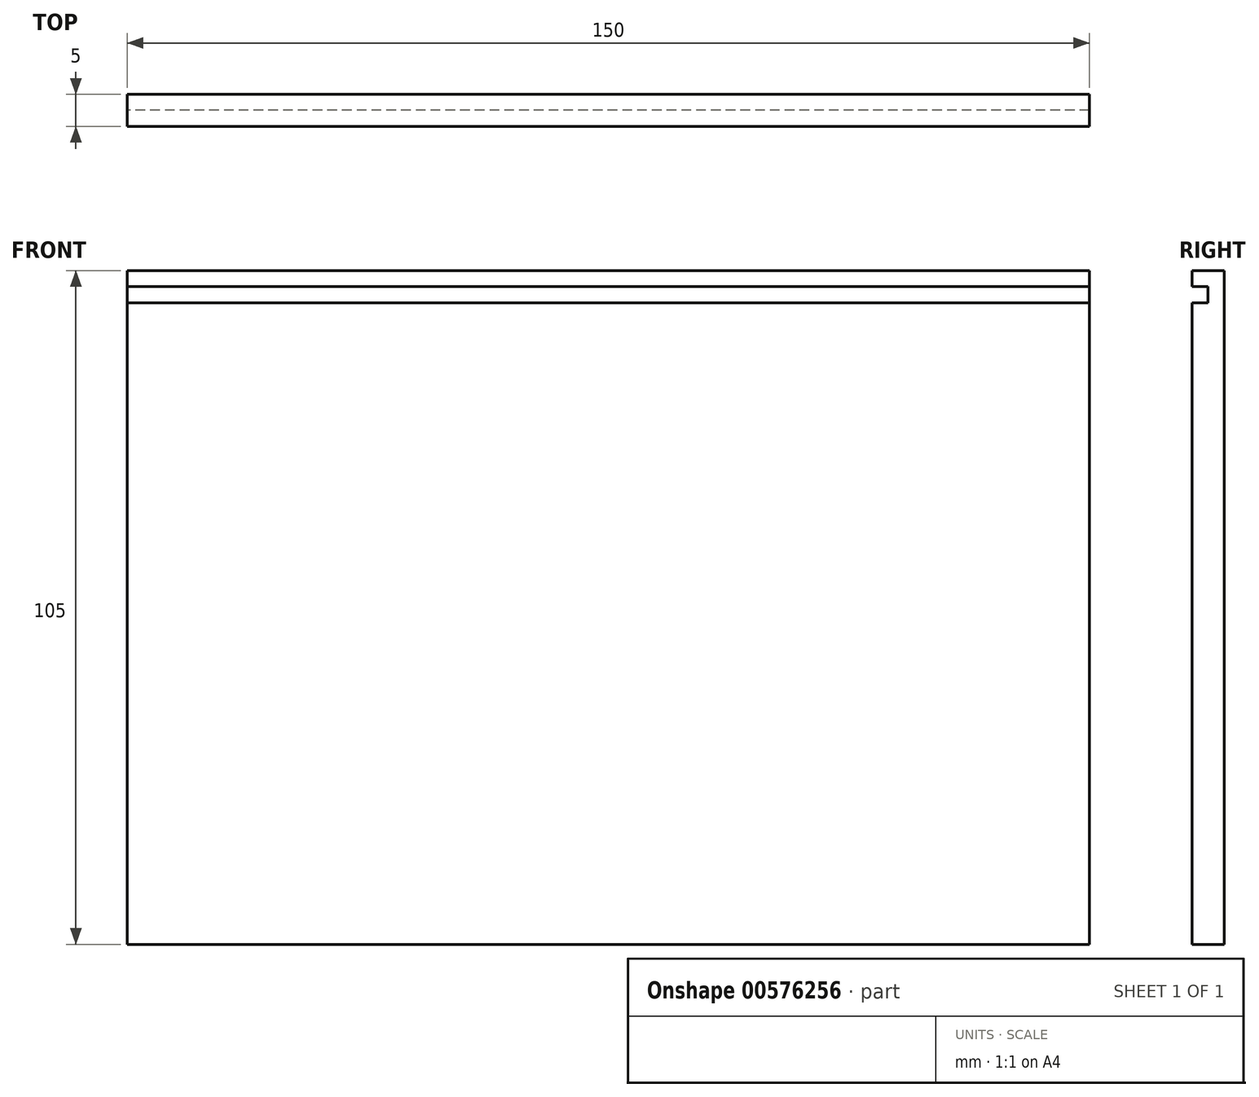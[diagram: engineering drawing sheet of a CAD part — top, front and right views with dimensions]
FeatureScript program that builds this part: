
annotation { "Feature Type Name" : "Feature", "Feature Type Description" : "" }
export const myFeature = defineFeature(function(context is Context, id is Id, definition is map)
    precondition{}
    {
        {
            var Q0;
            Q0=qCreatedBy(makeId("Front.planeOp"),FACE);
            var sketch = newSketch(context, id + "F0", { "sketchPlane" : qUnion([Q0])});
            skLineSegment(sketch, "E0.bottom", {"start": v(75, -52.5) * mm, "end": v(-75, -52.5) * mm});
            skLineSegment(sketch, "E0.top", {"start": v(75, 52.5) * mm, "end": v(-75, 52.5) * mm});
            skLineSegment(sketch, "E0.left", {"start": v(75, -52.5) * mm, "end": v(75, 52.5) * mm});
            skLineSegment(sketch, "E0.right", {"start": v(-75, -52.5) * mm, "end": v(-75, 52.5) * mm});
            skPoint(sketch, "E0.middle", {"position": v(0, 0) * mm});
            skSolve(sketch);
        }
        {
            var Q0;
            Q0=qSketchRegion(id+"F0",true);
            extrude(context, id + "F1", {"entities" : qUnion([Q0]), "depth" : 5 * mm, "offsetDistance" : 25 * mm});
        }
        {
            var Q0;
            Q0=makeQuery(id+"F1.opExtrude","CAP_FACE",FACE,{"disambiguationData":[OSD([sQuery(id+"F0.wireOp",EDGE,"E0.bottom"),sQuery(id+"F0.wireOp",EDGE,"E0.top"),sQuery(id+"F0.wireOp",EDGE,"E0.left"),sQuery(id+"F0.wireOp",EDGE,"E0.right")])],"isStart":false});
            var sketch = newSketch(context, id + "F2", { "sketchPlane" : qUnion([Q0])});
            skLineSegment(sketch, "E1", {"start": v(75, 50) * mm, "end": v(75, 47.5) * mm});
            skLineSegment(sketch, "E2", {"start": v(75, 47.5) * mm, "end": v(-75, 47.5) * mm});
            skLineSegment(sketch, "E3", {"start": v(-75, 47.5) * mm, "end": v(-75, 50) * mm});
            skLineSegment(sketch, "E4", {"start": v(-75, 50) * mm, "end": v(75, 50) * mm});
            skSolve(sketch);
        }
        {
            var Q0;
            Q0=makeQuery(id+"F2.imprint","IMPRINT",FACE,{"disambiguationData":[TD([[makeQuery(id+"F2.imprint","IMPRINT",EDGE,{"derivedFrom":sQuery(id+"F2.wireOp",EDGE,"E1")}),1.0]])]});
            extrude(context, id + "F3", {"entities" : qUnion([Q0]), "operationType" : NewBodyOperationType.REMOVE, "oppositeDirection" : true, "depth" : 2.5 * mm, "offsetDistance" : 25 * mm});
        }
    });
